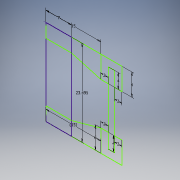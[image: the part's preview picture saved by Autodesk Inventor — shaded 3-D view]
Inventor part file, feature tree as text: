
AUTODESK INVENTOR PART (.ipt)
format: ipt  version: 2016 (Build 200138000, 138)  size: 111,104 bytes
history: native  units: mm
features: sketch x1
ambient origin geometry x8: Origin, YZ Plane, XZ Plane, XY Plane, X Axis, Y Axis, Z Axis, Center Point
feature tree (1):
  sketch  "Sketch1"  dims[d0=23.495mm d1=7.0mm d2=4.0mm d3=2.0mm d4=6.0mm d5=2.0mm d6=4.0mm d7=2.0mm d8=6.0mm d9=2.0mm d10=15.0mm d11=15.0mm]
